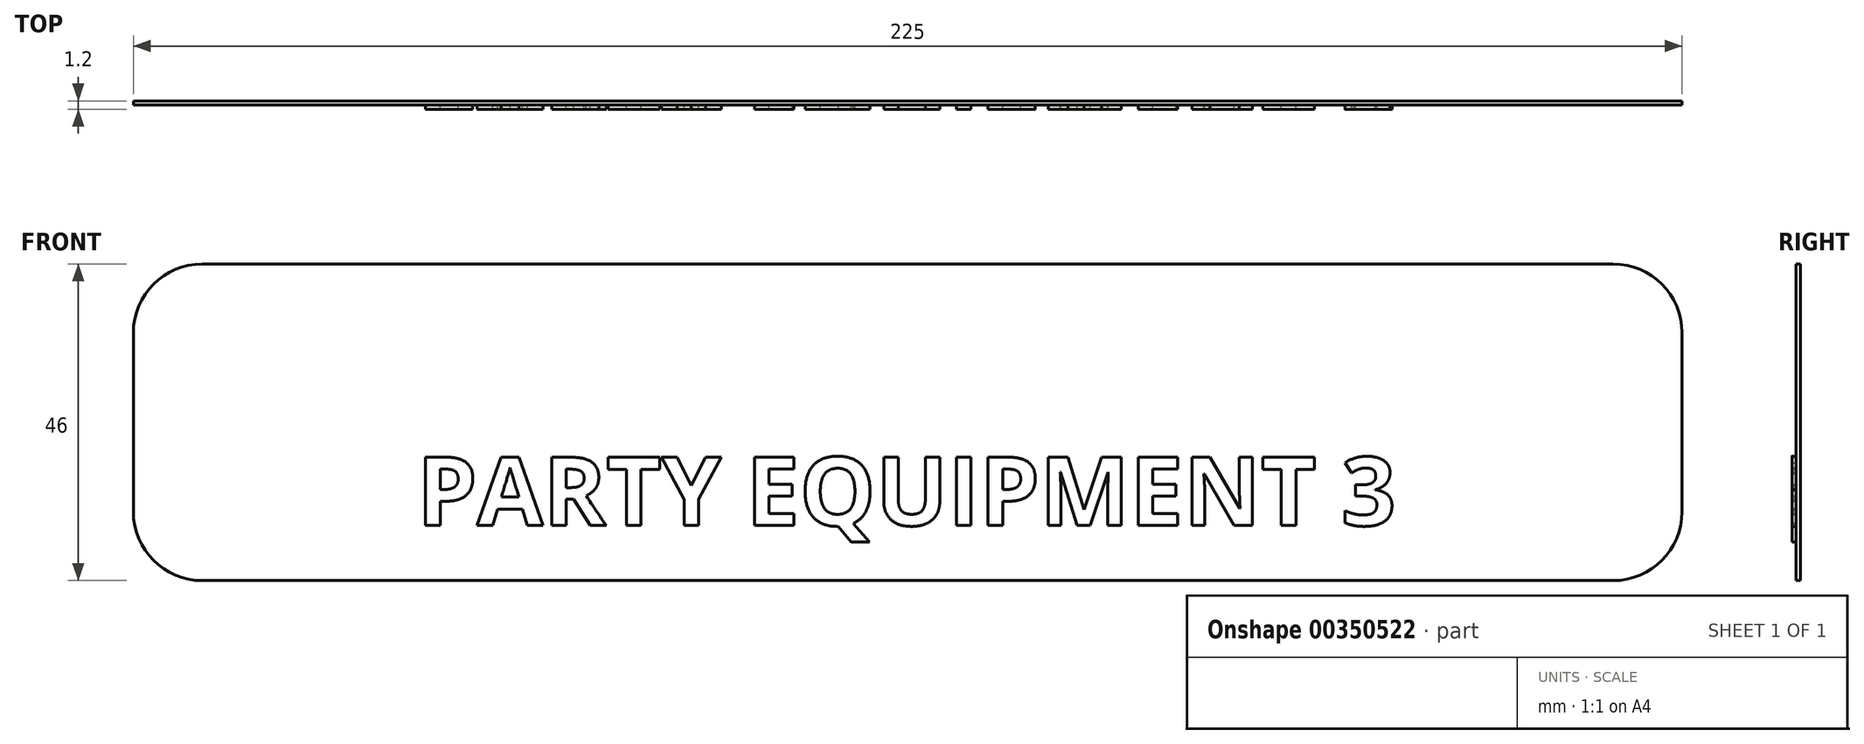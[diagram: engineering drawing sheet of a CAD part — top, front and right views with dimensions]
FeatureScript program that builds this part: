
annotation { "Feature Type Name" : "Feature", "Feature Type Description" : "" }
export const myFeature = defineFeature(function(context is Context, id is Id, definition is map)
    precondition{}
    {
        {
            var Q0;
            Q0=qCreatedBy(makeId("Front.planeOp"),FACE);
            var sketch = newSketch(context, id + "F0", { "sketchPlane" : qUnion([Q0])});
            skLineSegment(sketch, "E0.bottom", {"start": v(10, 0) * mm, "end": v(215, 0) * mm});
            skLineSegment(sketch, "E0.top", {"start": v(10, 46) * mm, "end": v(215, 46) * mm});
            skLineSegment(sketch, "E0.left", {"start": v(0, 10) * mm, "end": v(0, 36) * mm});
            skLineSegment(sketch, "E0.right", {"start": v(225, 10) * mm, "end": v(225, 36) * mm});
            skPoint(sketch, "E1.visualSharp", {"position": v(0, 46) * mm});
            skArc(sketch, "E1.filletArc", {"start": v(10, 46) * mm, "mid": v(2.93, 43.07) * mm, "end": v(0, 36) * mm});
            skPoint(sketch, "E2.visualSharp", {"position": v(0, 0) * mm});
            skArc(sketch, "E2.filletArc", {"start": v(0, 10) * mm, "mid": v(2.93, 2.93) * mm, "end": v(10, 0) * mm});
            skPoint(sketch, "E3.visualSharp", {"position": v(225, 46) * mm});
            skArc(sketch, "E3.filletArc", {"start": v(225, 36) * mm, "mid": v(222.07, 43.07) * mm, "end": v(215, 46) * mm});
            skPoint(sketch, "E4.visualSharp", {"position": v(225, 0) * mm});
            skArc(sketch, "E4.filletArc", {"start": v(215, 0) * mm, "mid": v(222.07, 2.93) * mm, "end": v(225, 10) * mm});
            skSolve(sketch);
        }
        {
            var Q0;
            Q0 = qSketchRegion(id + "F0", true);
            extrude(context, id + "F1", {"entities" : qUnion([Q0]), "depth" : 0.6 * mm});
        }
        {
            var Q0;
            Q0=makeQuery(id+"F1.opExtrude","CAP_FACE",FACE,{"disambiguationData":[OSD([sQuery(id+"F0.wireOp",EDGE,"E0.bottom"),sQuery(id+"F0.wireOp",EDGE,"E0.top"),sQuery(id+"F0.wireOp",EDGE,"E0.left"),sQuery(id+"F0.wireOp",EDGE,"E0.right"),sQuery(id+"F0.wireOp",EDGE,"E1.filletArc"),sQuery(id+"F0.wireOp",EDGE,"E2.filletArc"),sQuery(id+"F0.wireOp",EDGE,"E3.filletArc"),sQuery(id+"F0.wireOp",EDGE,"E4.filletArc")])],"isStart":false});
            var sketch = newSketch(context, id + "F2", { "sketchPlane" : qUnion([Q0])});
            skText(sketch, "E5", { "text": "PARTY EQUIPMENT 3", "fontName": "OpenSans-Bold.ttf"});
            const initialGuessF2  = {"E5": [0.04122, 0.008, 1, 0, 0.01]};
            skSetInitialGuess(sketch, initialGuessF2);
            skSolve(sketch);
        }
        {
            var Q0;
            Q0 = qSketchRegion(id + "F2", true);
            extrude(context, id + "F3", {"entities" : qUnion([Q0]), "operationType" : NewBodyOperationType.ADD, "depth" : 0.6 * mm});
        }
    });
